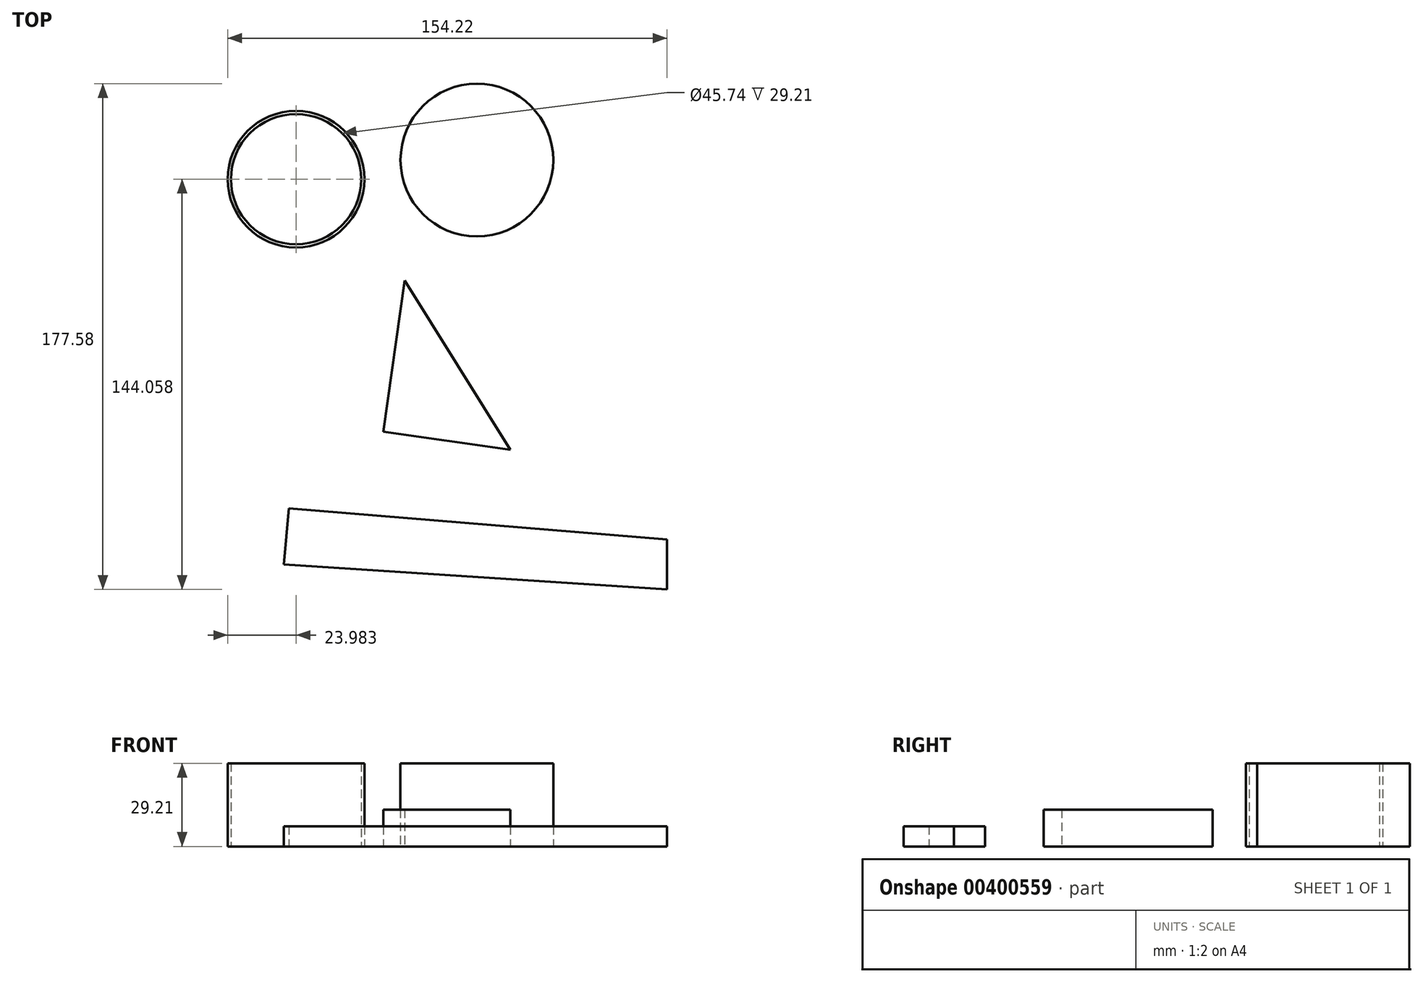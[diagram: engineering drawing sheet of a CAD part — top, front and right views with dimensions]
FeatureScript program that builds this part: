
annotation { "Feature Type Name" : "Feature", "Feature Type Description" : "" }
export const myFeature = defineFeature(function(context is Context, id is Id, definition is map)
    precondition{}
    {
        {
            var Q0;
            Q0=qCreatedBy(makeId("Top.planeOp"),FACE);
            var sketch = newSketch(context, id + "F0", { "sketchPlane" : qUnion([Q0])});
            skCircle(sketch, "E0", {"center": v(-73.14, 6.79) * mm, "radius": 22.87 * mm});
            skCircle(sketch, "E1", {"center": v(-9.67, 13.5) * mm, "radius": 26.8 * mm});
            skCircle(sketch, "E2", {"center": v(-73.14, 6.79) * mm, "radius": 23.98 * mm});
            skSolve(sketch);
        }
        {
            var Q0;
            Q0 = qSketchRegion(id + "F0", true);
            extrude(context, id + "F1", {"entities" : qUnion([Q0]), "depth" : 29.2 * mm});
        }
        {
            var Q0;
            Q0=qCreatedBy(makeId("Top.planeOp"),FACE);
            var sketch = newSketch(context, id + "F2", { "sketchPlane" : qUnion([Q0])});
            skLineSegment(sketch, "E3", {"start": v(-35, -28.81) * mm, "end": v(-42.56, -81.82) * mm});
            skLineSegment(sketch, "E4", {"start": v(-42.56, -81.82) * mm, "end": v(5, -88.6) * mm});
            skLineSegment(sketch, "E5", {"start": v(4.5, -92.06) * mm, "end": v(-35, -28.81) * mm});
            skSolve(sketch);
        }
        {
            var Q0;
            Q0 = qSketchRegion(id + "F2", true);
            extrude(context, id + "F3", {"entities" : qUnion([Q0]), "depth" : 12.95 * mm});
        }
        {
            var Q0;
            Q0=qCreatedBy(makeId("Top.planeOp"),FACE);
            var sketch = newSketch(context, id + "F4", { "sketchPlane" : qUnion([Q0])});
            skLineSegment(sketch, "E6", {"start": v(-75.66, -108.77) * mm, "end": v(57.1, -119.67) * mm});
            skLineSegment(sketch, "E7", {"start": v(57.1, -119.67) * mm, "end": v(71.79, -141.87) * mm});
            skLineSegment(sketch, "E8", {"start": v(71.79, -141.87) * mm, "end": v(67.08, -150.57) * mm});
            skLineSegment(sketch, "E9", {"start": v(67.08, -150.57) * mm, "end": v(57.1, -137.27) * mm});
            skLineSegment(sketch, "E10", {"start": v(57.1, -137.27) * mm, "end": v(57.1, -119.67) * mm});
            skLineSegment(sketch, "E11", {"start": v(57.1, -137.27) * mm, "end": v(-77.38, -128.47) * mm});
            skPoint(sketch, "E11.endSnap0", {"position": v(57.1, -128.47) * mm});
            skLineSegment(sketch, "E12", {"start": v(-75.66, -108.77) * mm, "end": v(-77.38, -128.47) * mm});
            skLineSegment(sketch, "E13", {"start": v(-77.38, -128.47) * mm, "end": v(-56.75, -157.72) * mm});
            skLineSegment(sketch, "E14", {"start": v(-56.8, -157) * mm, "end": v(67.08, -150.57) * mm});
            skLineSegment(sketch, "E15", {"start": v(-56.75, -129.82) * mm, "end": v(-46.91, -150.57) * mm});
            skLineSegment(sketch, "E16", {"start": v(-46.9, -147.52) * mm, "end": v(-33.9, -148.37) * mm});
            skLineSegment(sketch, "E17", {"start": v(-34.17, -146.93) * mm, "end": v(-43.32, -130.7) * mm});
            skSolve(sketch);
        }
        {
            var Q0;
            Q0=makeQuery(id+"F4.imprint","IMPRINT",FACE,{"disambiguationData":[TD([[makeQuery(id+"F4.imprint","IMPRINT",EDGE,{"derivedFrom":sQuery(id+"F4.wireOp",EDGE,"E6")}),-1.0]])]});
            extrude(context, id + "F5", {"entities" : qUnion([Q0]), "depth" : 7.11 * mm});
        }
    });
